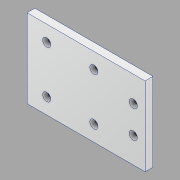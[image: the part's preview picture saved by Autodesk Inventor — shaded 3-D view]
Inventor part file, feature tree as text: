
AUTODESK INVENTOR PART (.ipt)
format: ipt  version: 2020 (Build 240168000, 168)  size: 115,712 bytes
history: native  units: in
note: dims shown in document units (in); Inventor stores cm internally (conversion verified against a paired STEP export)
features: sketch x2, other x1, extrude x1, hole x1
ambient origin geometry x8: Origin, YZ Plane, XZ Plane, XY Plane, X Axis, Y Axis, Z Axis, Center Point
bodies: Body1 (feature_tree)
feature tree (5):
  other  "Sólido1"
  extrude  "Extrusión1"  Depth=2.5in
  hole  "Agujero1"  [1 undecoded]
  sketch  "Boceto1"  dims[d0=3.75in d1=2.5in]
  sketch  "Boceto2"  dims[d2=0.25in d3=0.0in d4=0.375in d5=1.25in d6=1.5in d7=0.375in d8=1.25in d9=1.5in d10=2.5in d11=1.25in d12=0.875in d13=0.4375in d14=1.5in d15=1.5in d16=0.75in d17=0.75in d18=0.0979in d19=0.25in d20=0.26in d21=0.0118in d22=0.5635in d23=0.375in d24=0.8108in]
note: 1 required parameter value undecoded (feature->parameter linkage not recoverable at this tier; creation-order binding heuristic only, values carry confidence <= 0.55)
